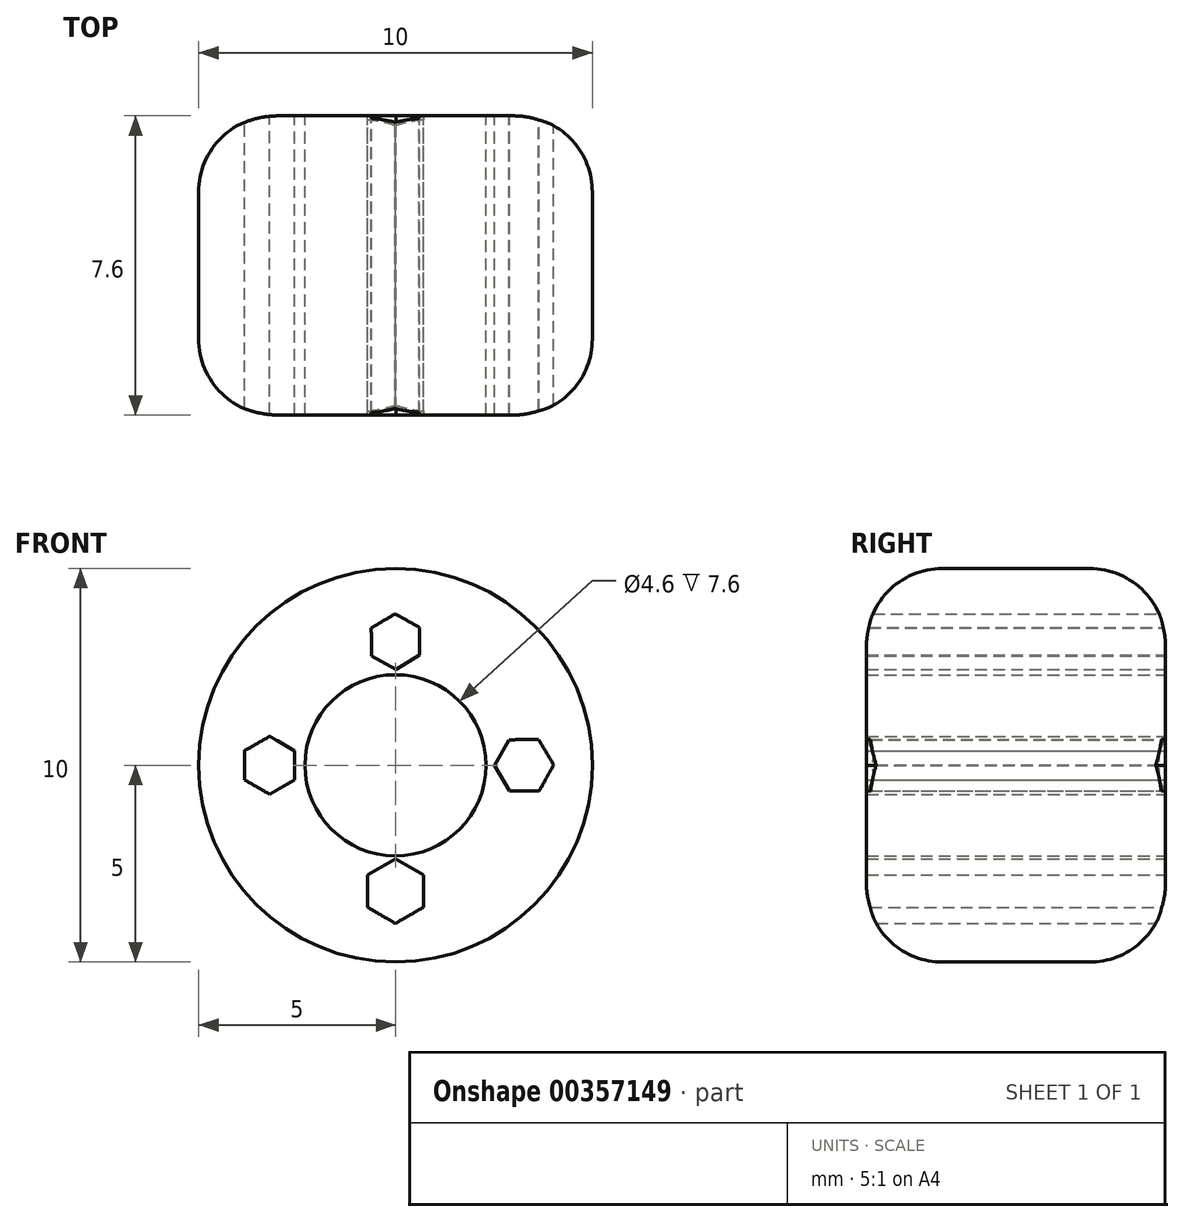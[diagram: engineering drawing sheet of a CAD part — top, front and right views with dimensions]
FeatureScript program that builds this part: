
annotation { "Feature Type Name" : "Feature", "Feature Type Description" : "" }
export const myFeature = defineFeature(function(context is Context, id is Id, definition is map)
    precondition{}
    {
        {
            var Q0;
            Q0=qCreatedBy(makeId("Front.planeOp"),FACE);
            var sketch = newSketch(context, id + "F0", { "sketchPlane" : qUnion([Q0])});
            skCircle(sketch, "E0", {"center": v(0, 0) * mm, "radius": 5 * mm});
            skCircle(sketch, "E1.cCircle", {"center": v(0, 3.14) * mm, "radius": 0.61 * mm, "construction": true});
            skLineSegment(sketch, "E1.0", {"start": v(0.62, 2.8) * mm, "end": v(0.01, 2.44) * mm});
            skLineSegment(sketch, "E1.1", {"start": v(0.01, 2.44) * mm, "end": v(-0.6, 2.78) * mm});
            skLineSegment(sketch, "E1.2", {"start": v(-0.6, 2.78) * mm, "end": v(-0.62, 3.49) * mm});
            skLineSegment(sketch, "E1.3", {"start": v(-0.62, 3.49) * mm, "end": v(-0.01, 3.85) * mm});
            skLineSegment(sketch, "E1.4", {"start": v(-0.01, 3.85) * mm, "end": v(0.6, 3.5) * mm});
            skLineSegment(sketch, "E1.5", {"start": v(0.6, 3.5) * mm, "end": v(0.62, 2.8) * mm});
            skPoint(sketch, "E1.0.midPoint", {"position": v(0.31, 2.62) * mm});
            skCircle(sketch, "E2.cCircle", {"center": v(3.27, 0) * mm, "radius": 0.65 * mm, "construction": true});
            skLineSegment(sketch, "E2.0", {"start": v(2.51, -0.01) * mm, "end": v(2.88, 0.65) * mm});
            skLineSegment(sketch, "E2.1", {"start": v(2.88, 0.65) * mm, "end": v(3.63, 0.66) * mm});
            skLineSegment(sketch, "E2.2", {"start": v(3.63, 0.66) * mm, "end": v(4.02, 0.01) * mm});
            skLineSegment(sketch, "E2.3", {"start": v(4.02, 0.01) * mm, "end": v(3.65, -0.65) * mm});
            skLineSegment(sketch, "E2.4", {"start": v(3.65, -0.65) * mm, "end": v(2.9, -0.66) * mm});
            skLineSegment(sketch, "E2.5", {"start": v(2.9, -0.66) * mm, "end": v(2.51, -0.01) * mm});
            skPoint(sketch, "E2.0.midPoint", {"position": v(2.7, 0.32) * mm});
            skCircle(sketch, "E3.cCircle", {"center": v(-3.2, 0) * mm, "radius": 0.64 * mm, "construction": true});
            skLineSegment(sketch, "E3.0", {"start": v(-2.56, 0.37) * mm, "end": v(-2.56, -0.37) * mm});
            skLineSegment(sketch, "E3.1", {"start": v(-2.56, -0.37) * mm, "end": v(-3.2, -0.74) * mm});
            skLineSegment(sketch, "E3.2", {"start": v(-3.2, -0.74) * mm, "end": v(-3.83, -0.37) * mm});
            skLineSegment(sketch, "E3.3", {"start": v(-3.83, -0.37) * mm, "end": v(-3.83, 0.37) * mm});
            skLineSegment(sketch, "E3.4", {"start": v(-3.83, 0.37) * mm, "end": v(-3.2, 0.74) * mm});
            skLineSegment(sketch, "E3.5", {"start": v(-3.2, 0.74) * mm, "end": v(-2.56, 0.37) * mm});
            skPoint(sketch, "E3.0.midPoint", {"position": v(-2.56, 0) * mm});
            skCircle(sketch, "E4", {"center": v(0, 0) * mm, "radius": 2.3 * mm});
            skCircle(sketch, "E5.cCircle", {"center": v(0, -3.2) * mm, "radius": 0.7 * mm, "construction": true});
            skLineSegment(sketch, "E5.0", {"start": v(-0.7, -3.6) * mm, "end": v(-0.7, -2.8) * mm});
            skLineSegment(sketch, "E5.1", {"start": v(-0.7, -2.8) * mm, "end": v(0, -2.38) * mm});
            skLineSegment(sketch, "E5.2", {"start": v(0, -2.38) * mm, "end": v(0.7, -2.8) * mm});
            skLineSegment(sketch, "E5.3", {"start": v(0.7, -2.8) * mm, "end": v(0.7, -3.6) * mm});
            skLineSegment(sketch, "E5.4", {"start": v(0.7, -3.6) * mm, "end": v(0, -4.02) * mm});
            skLineSegment(sketch, "E5.5", {"start": v(0, -4.02) * mm, "end": v(-0.7, -3.6) * mm});
            skPoint(sketch, "E5.0.midPoint", {"position": v(-0.7, -3.2) * mm});
            skSolve(sketch);
        }
        {
            var Q0;
            Q0=makeQuery(id+"F0.imprint","IMPRINT",FACE,{"disambiguationData":[TD([[makeQuery(id+"F0.imprint","IMPRINT",EDGE,{"derivedFrom":sQuery(id+"F0.wireOp",EDGE,"E0")}),1.0]])]});
            extrude(context, id + "F1", {"entities" : qUnion([Q0]), "endBound" : BoundingType.SYMMETRIC, "depth" : 7.6 * mm});
        }
        {
            var Q0;
            Q0=makeQuery(id+"F1.opExtrude","SWEPT_FACE",FACE,{"disambiguationData":[OSD([sQuery(id+"F0.wireOp",EDGE,"E0")])]});
            fillet(context, id + "F2", {"entities" : qUnion([Q0]), "radius" : 1.93 * mm, "tangentPropagation" : true, "allowEdgeOverflow" : false});
        }
    });
